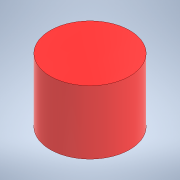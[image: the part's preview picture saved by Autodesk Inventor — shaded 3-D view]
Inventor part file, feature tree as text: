
AUTODESK INVENTOR PART (.ipt)
format: ipt  version: 2021 (Build 250183000, 183)  size: 100,864 bytes
history: native  units: mm
features: revolve x1, sketch x1
ambient origin geometry x8: Origin, YZ Plane, XZ Plane, XY Plane, X Axis, Y Axis, Z Axis, Center Point
bodies: Solid1 (feature_tree)
feature tree (2):
  revolve  "Revolution1"  [1 undecoded]
  sketch  "Sketch1"  dims[d0=40.0mm d1=20.0mm d2=0.0mm d3=11.665mm d4=0.0mm d5=25.0mm d6=90.0deg]
note: 1 required parameter value undecoded (feature->parameter linkage not recoverable at this tier; creation-order binding heuristic only, values carry confidence <= 0.55)
